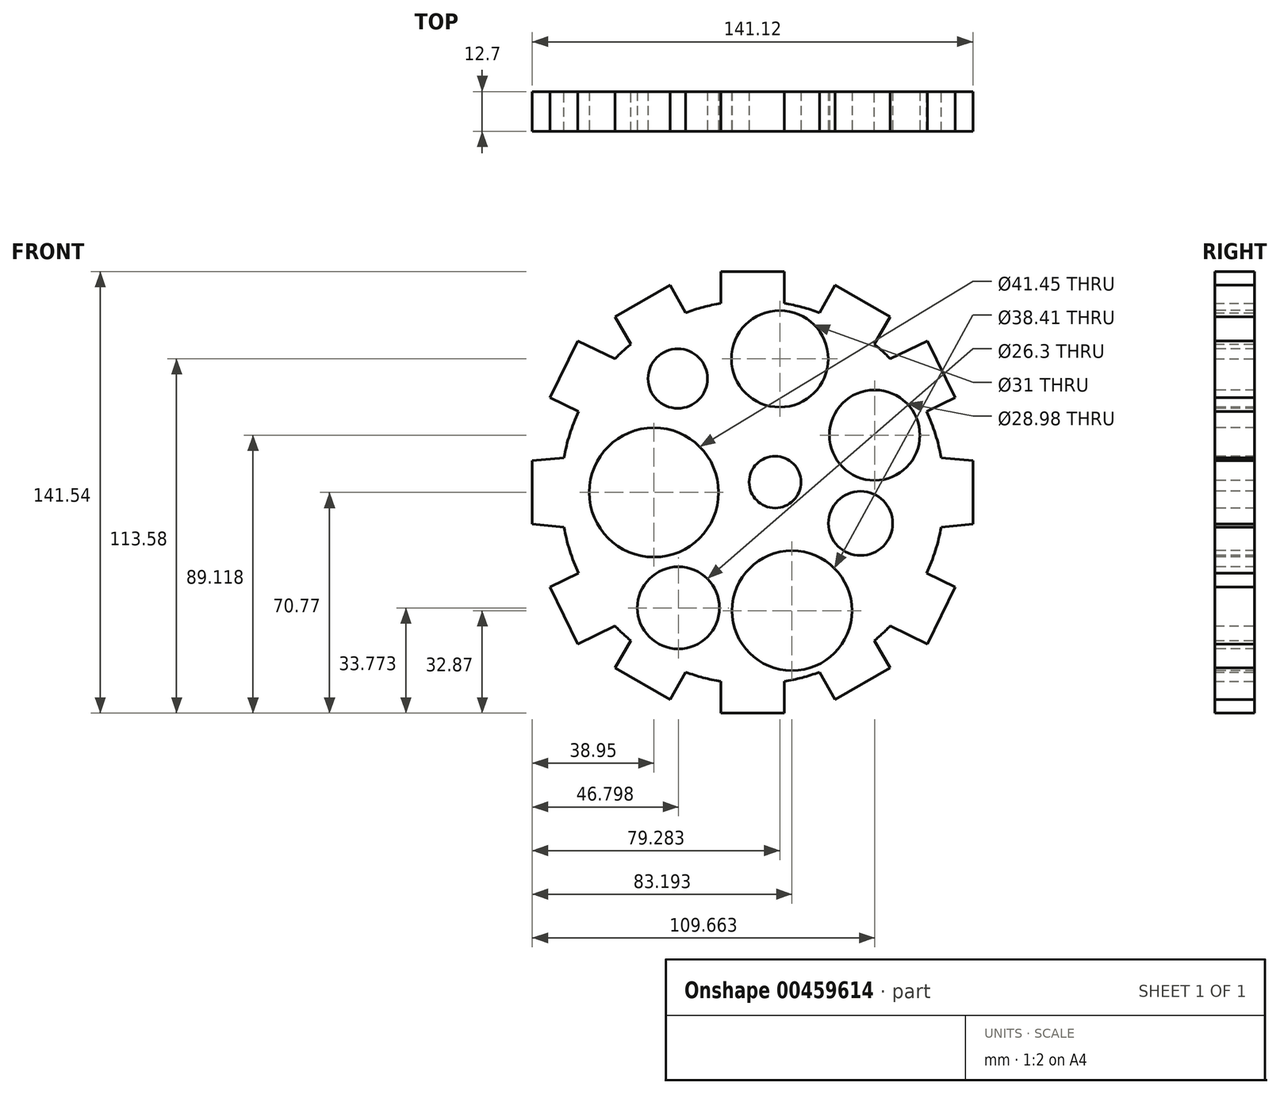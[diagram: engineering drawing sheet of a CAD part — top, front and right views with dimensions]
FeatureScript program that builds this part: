
annotation { "Feature Type Name" : "Feature", "Feature Type Description" : "" }
export const myFeature = defineFeature(function(context is Context, id is Id, definition is map)
    precondition{}
    {
        {
            var Q0;
            Q0=qCreatedBy(makeId("Front.planeOp"),FACE);
            var sketch = newSketch(context, id + "F0", { "sketchPlane" : qUnion([Q0])});
            skArc(sketch, "E0", {"start": v(-55.74, 25.88) * mm, "mid": v(-58.56, 18.64) * mm, "end": v(-60.44, 11.1) * mm});
            skLineSegment(sketch, "E1", {"start": v(-70.56, 0) * mm, "end": v(-70.56, 10.16) * mm});
            skLineSegment(sketch, "E2", {"start": v(-55.74, 25.88) * mm, "end": v(-64.87, 30.33) * mm});
            skLineSegment(sketch, "E3", {"start": v(-64.87, 30.33) * mm, "end": v(-55.97, 48.6) * mm});
            skLineSegment(sketch, "E4", {"start": v(-55.97, 48.6) * mm, "end": v(-44.1, 42.8) * mm});
            skLineSegment(sketch, "E5", {"start": v(-70.56, 10.16) * mm, "end": v(-60.44, 11.1) * mm});
            skLineSegment(sketch, "E6", {"start": v(-39.04, 47.46) * mm, "end": v(-44.1, 56.28) * mm});
            skLineSegment(sketch, "E7", {"start": v(-44.1, 56.28) * mm, "end": v(-26.46, 66.39) * mm});
            skLineSegment(sketch, "E8", {"start": v(-26.46, 66.39) * mm, "end": v(-21.42, 57.6) * mm});
            skArc(sketch, "E9.trimOffspring", {"start": v(-39.04, 47.46) * mm, "mid": v(-41.63, 45.2) * mm, "end": v(-44.1, 42.8) * mm});
            skLineSegment(sketch, "E10", {"start": v(-10.16, 60.6) * mm, "end": v(-10.16, 70.77) * mm});
            skLineSegment(sketch, "E11", {"start": v(-10.16, 70.77) * mm, "end": v(0, 70.77) * mm});
            skLineSegment(sketch, "E12.MirrorCS", {"start": v(10.16, 70.77) * mm, "end": v(0, 70.77) * mm});
            skLineSegment(sketch, "E13.MirrorCS", {"start": v(10.16, 60.6) * mm, "end": v(10.16, 70.77) * mm});
            skLineSegment(sketch, "E14.MirrorCS", {"start": v(44.1, 56.28) * mm, "end": v(26.46, 66.39) * mm});
            skLineSegment(sketch, "E15.MirrorCS", {"start": v(26.46, 66.39) * mm, "end": v(21.42, 57.6) * mm});
            skLineSegment(sketch, "E16.MirrorCS", {"start": v(39.04, 47.46) * mm, "end": v(44.1, 56.28) * mm});
            skLineSegment(sketch, "E17.MirrorCS", {"start": v(55.97, 48.6) * mm, "end": v(44.1, 42.8) * mm});
            skLineSegment(sketch, "E18.MirrorCS", {"start": v(64.87, 30.33) * mm, "end": v(55.97, 48.6) * mm});
            skLineSegment(sketch, "E19.MirrorCS", {"start": v(55.74, 25.88) * mm, "end": v(64.87, 30.33) * mm});
            skArc(sketch, "E20.MirrorCS", {"start": v(55.74, 25.88) * mm, "mid": v(58.56, 18.64) * mm, "end": v(60.44, 11.1) * mm});
            skLineSegment(sketch, "E21.MirrorCS", {"start": v(70.56, 10.16) * mm, "end": v(60.44, 11.1) * mm});
            skLineSegment(sketch, "E22.MirrorCS", {"start": v(70.56, 0) * mm, "end": v(70.56, 10.16) * mm});
            skArc(sketch, "E23.trimOffspring", {"start": v(-44.1, 42.8) * mm, "mid": v(-41.63, 45.2) * mm, "end": v(-39.04, 47.46) * mm});
            skArc(sketch, "E24.trimOffspring", {"start": v(-21.42, 57.6) * mm, "mid": v(-15.86, 59.37) * mm, "end": v(-10.16, 60.6) * mm});
            skArc(sketch, "E25.trimOffspring", {"start": v(-10.16, 60.6) * mm, "mid": v(-15.86, 59.37) * mm, "end": v(-21.42, 57.6) * mm});
            skArc(sketch, "E26.trimOffspring", {"start": v(21.42, 57.6) * mm, "mid": v(15.86, 59.37) * mm, "end": v(10.16, 60.6) * mm});
            skArc(sketch, "E27.trimOffspring", {"start": v(44.1, 42.8) * mm, "mid": v(41.63, 45.2) * mm, "end": v(39.04, 47.46) * mm});
            skLineSegment(sketch, "E28.MirrorCS", {"start": v(-70.56, 0) * mm, "end": v(-70.56, -10.16) * mm});
            skLineSegment(sketch, "E29.MirrorCS", {"start": v(-70.56, -10.16) * mm, "end": v(-60.44, -11.1) * mm});
            skLineSegment(sketch, "E30.MirrorCS", {"start": v(-55.74, -25.88) * mm, "end": v(-64.87, -30.33) * mm});
            skLineSegment(sketch, "E31.MirrorCS", {"start": v(-64.87, -30.33) * mm, "end": v(-55.97, -48.6) * mm});
            skLineSegment(sketch, "E32.MirrorCS", {"start": v(-55.97, -48.6) * mm, "end": v(-44.1, -42.8) * mm});
            skLineSegment(sketch, "E33.MirrorCS", {"start": v(-39.04, -47.46) * mm, "end": v(-44.1, -56.28) * mm});
            skLineSegment(sketch, "E34.MirrorCS", {"start": v(-44.1, -56.28) * mm, "end": v(-26.46, -66.39) * mm});
            skLineSegment(sketch, "E35.MirrorCS", {"start": v(-26.46, -66.39) * mm, "end": v(-21.42, -57.6) * mm});
            skLineSegment(sketch, "E36.MirrorCS", {"start": v(-10.16, -60.6) * mm, "end": v(-10.16, -70.77) * mm});
            skLineSegment(sketch, "E37.MirrorCS", {"start": v(-10.16, -70.77) * mm, "end": v(0, -70.77) * mm});
            skLineSegment(sketch, "E38.MirrorCS", {"start": v(10.16, -70.77) * mm, "end": v(0, -70.77) * mm});
            skLineSegment(sketch, "E39.MirrorCS", {"start": v(10.16, -60.6) * mm, "end": v(10.16, -70.77) * mm});
            skLineSegment(sketch, "E40.MirrorCS", {"start": v(26.46, -66.39) * mm, "end": v(21.42, -57.6) * mm});
            skLineSegment(sketch, "E41.MirrorCS", {"start": v(44.1, -56.28) * mm, "end": v(26.46, -66.39) * mm});
            skLineSegment(sketch, "E42.MirrorCS", {"start": v(39.04, -47.46) * mm, "end": v(44.1, -56.28) * mm});
            skLineSegment(sketch, "E43.MirrorCS", {"start": v(55.97, -48.6) * mm, "end": v(44.1, -42.8) * mm});
            skLineSegment(sketch, "E44.MirrorCS", {"start": v(64.87, -30.33) * mm, "end": v(55.97, -48.6) * mm});
            skLineSegment(sketch, "E45.MirrorCS", {"start": v(55.74, -25.88) * mm, "end": v(64.87, -30.33) * mm});
            skLineSegment(sketch, "E46.MirrorCS", {"start": v(70.56, -10.16) * mm, "end": v(60.44, -11.1) * mm});
            skLineSegment(sketch, "E47.MirrorCS", {"start": v(70.56, 0) * mm, "end": v(70.56, -10.16) * mm});
            skArc(sketch, "E48.trimOffspring", {"start": v(-60.44, 11.1) * mm, "mid": v(-58.56, 18.64) * mm, "end": v(-55.74, 25.88) * mm});
            skArc(sketch, "E49.trimOffspring", {"start": v(-60.44, -11.1) * mm, "mid": v(-58.56, -18.64) * mm, "end": v(-55.74, -25.88) * mm});
            skArc(sketch, "E50.trimOffspring", {"start": v(-55.74, -25.88) * mm, "mid": v(-58.56, -18.64) * mm, "end": v(-60.44, -11.1) * mm});
            skArc(sketch, "E51.trimOffspring", {"start": v(-44.1, -42.8) * mm, "mid": v(-41.63, -45.2) * mm, "end": v(-39.04, -47.46) * mm});
            skArc(sketch, "E52.trimOffspring", {"start": v(-21.42, -57.6) * mm, "mid": v(-15.86, -59.37) * mm, "end": v(-10.16, -60.6) * mm});
            skArc(sketch, "E53.trimOffspring", {"start": v(10.16, -60.6) * mm, "mid": v(15.86, -59.37) * mm, "end": v(21.42, -57.6) * mm});
            skArc(sketch, "E54.trimOffspring", {"start": v(-10.16, -60.6) * mm, "mid": v(-15.86, -59.37) * mm, "end": v(-21.42, -57.6) * mm});
            skArc(sketch, "E55.trimOffspring", {"start": v(21.42, -57.6) * mm, "mid": v(15.86, -59.37) * mm, "end": v(10.16, -60.6) * mm});
            skArc(sketch, "E56.trimOffspring", {"start": v(44.1, -42.8) * mm, "mid": v(41.63, -45.2) * mm, "end": v(39.04, -47.46) * mm});
            skArc(sketch, "E57.trimOffspring", {"start": v(39.04, -47.46) * mm, "mid": v(41.63, -45.2) * mm, "end": v(44.1, -42.8) * mm});
            skArc(sketch, "E58.trimOffspring", {"start": v(55.74, -25.88) * mm, "mid": v(58.56, -18.64) * mm, "end": v(60.44, -11.1) * mm});
            skArc(sketch, "E59.trimOffspring", {"start": v(60.44, -11.1) * mm, "mid": v(58.56, -18.64) * mm, "end": v(55.74, -25.88) * mm});
            skArc(sketch, "E60.trimOffspring", {"start": v(60.44, 11.1) * mm, "mid": v(58.56, 18.64) * mm, "end": v(55.74, 25.88) * mm});
            skArc(sketch, "E61.trimOffspring", {"start": v(10.16, 60.6) * mm, "mid": v(15.86, 59.37) * mm, "end": v(21.42, 57.6) * mm});
            skLineSegment(sketch, "E62.trimOffspring", {"start": v(0, -70.77) * mm, "end": v(0, -71.89) * mm, "construction": true});
            skPoint(sketch, "E63.start.orphan", {"position": v(0, 76.4) * mm});
            skPoint(sketch, "E64.start.orphan", {"position": v(-89.94, 0) * mm});
            skSolve(sketch);
        }
        {
            var Q0;
            Q0 = qSketchRegion(id + "F0", true);
            extrude(context, id + "F1", {"entities" : qUnion([Q0]), "depth" : 12.7 * mm});
        }
        {
            var Q0;
            Q0=makeQuery(id+"F1.opExtrude","CAP_FACE",FACE,{"disambiguationData":[OSD([sQuery(id+"F0.wireOp",EDGE,"E1"),sQuery(id+"F0.wireOp",EDGE,"E2"),sQuery(id+"F0.wireOp",EDGE,"E3"),sQuery(id+"F0.wireOp",EDGE,"E4"),sQuery(id+"F0.wireOp",EDGE,"E5"),sQuery(id+"F0.wireOp",EDGE,"E6"),sQuery(id+"F0.wireOp",EDGE,"E7"),sQuery(id+"F0.wireOp",EDGE,"E8"),sQuery(id+"F0.wireOp",EDGE,"E10"),sQuery(id+"F0.wireOp",EDGE,"E11"),sQuery(id+"F0.wireOp",EDGE,"E12.MirrorCS"),sQuery(id+"F0.wireOp",EDGE,"E13.MirrorCS"),sQuery(id+"F0.wireOp",EDGE,"E14.MirrorCS"),sQuery(id+"F0.wireOp",EDGE,"E15.MirrorCS"),sQuery(id+"F0.wireOp",EDGE,"E16.MirrorCS"),sQuery(id+"F0.wireOp",EDGE,"E17.MirrorCS"),sQuery(id+"F0.wireOp",EDGE,"E18.MirrorCS"),sQuery(id+"F0.wireOp",EDGE,"E19.MirrorCS"),sQuery(id+"F0.wireOp",EDGE,"E21.MirrorCS"),sQuery(id+"F0.wireOp",EDGE,"E22.MirrorCS"),sQuery(id+"F0.wireOp",EDGE,"E23.trimOffspring"),sQuery(id+"F0.wireOp",EDGE,"E25.trimOffspring"),sQuery(id+"F0.wireOp",EDGE,"E27.trimOffspring"),sQuery(id+"F0.wireOp",EDGE,"E28.MirrorCS"),sQuery(id+"F0.wireOp",EDGE,"E29.MirrorCS"),sQuery(id+"F0.wireOp",EDGE,"E30.MirrorCS"),sQuery(id+"F0.wireOp",EDGE,"E31.MirrorCS"),sQuery(id+"F0.wireOp",EDGE,"E32.MirrorCS"),sQuery(id+"F0.wireOp",EDGE,"E33.MirrorCS"),sQuery(id+"F0.wireOp",EDGE,"E34.MirrorCS"),sQuery(id+"F0.wireOp",EDGE,"E35.MirrorCS"),sQuery(id+"F0.wireOp",EDGE,"E36.MirrorCS"),sQuery(id+"F0.wireOp",EDGE,"E37.MirrorCS"),sQuery(id+"F0.wireOp",EDGE,"E38.MirrorCS"),sQuery(id+"F0.wireOp",EDGE,"E39.MirrorCS"),sQuery(id+"F0.wireOp",EDGE,"E40.MirrorCS"),sQuery(id+"F0.wireOp",EDGE,"E41.MirrorCS"),sQuery(id+"F0.wireOp",EDGE,"E42.MirrorCS"),sQuery(id+"F0.wireOp",EDGE,"E43.MirrorCS"),sQuery(id+"F0.wireOp",EDGE,"E44.MirrorCS"),sQuery(id+"F0.wireOp",EDGE,"E45.MirrorCS"),sQuery(id+"F0.wireOp",EDGE,"E46.MirrorCS"),sQuery(id+"F0.wireOp",EDGE,"E47.MirrorCS"),sQuery(id+"F0.wireOp",EDGE,"E48.trimOffspring"),sQuery(id+"F0.wireOp",EDGE,"E50.trimOffspring"),sQuery(id+"F0.wireOp",EDGE,"E51.trimOffspring"),sQuery(id+"F0.wireOp",EDGE,"E54.trimOffspring"),sQuery(id+"F0.wireOp",EDGE,"E55.trimOffspring"),sQuery(id+"F0.wireOp",EDGE,"E57.trimOffspring"),sQuery(id+"F0.wireOp",EDGE,"E59.trimOffspring"),sQuery(id+"F0.wireOp",EDGE,"E60.trimOffspring"),sQuery(id+"F0.wireOp",EDGE,"E61.trimOffspring")])],"isStart":false});
            var sketch = newSketch(context, id + "F2", { "sketchPlane" : qUnion([Q0])});
            skLineSegment(sketch, "E65", {"start": v(0, 91.04) * mm, "end": v(0, -92.83) * mm, "construction": true});
            skLineSegment(sketch, "E66", {"start": v(-95.47, 0) * mm, "end": v(102.1, 0) * mm, "construction": true});
            skArc(sketch, "E67", {"start": v(-10.88, 0) * mm, "mid": v(-31.61, 20.73) * mm, "end": v(-52.34, 0) * mm});
            skArc(sketch, "E68.MirrorCS", {"start": v(-10.88, 0) * mm, "mid": v(-31.61, -20.73) * mm, "end": v(-52.34, 0) * mm});
            skSolve(sketch);
        }
        {
            var Q0;
            Q0=makeQuery(id+"F2.imprint","IMPRINT",FACE,{"disambiguationData":[TD([[makeQuery(id+"F2.imprint","IMPRINT",EDGE,{"derivedFrom":sQuery(id+"F2.wireOp",EDGE,"E67")}),1.0]])]});
            extrude(context, id + "F3", {"entities" : qUnion([Q0]), "operationType" : NewBodyOperationType.REMOVE, "oppositeDirection" : true, "depth" : 25.4 * mm});
        }
        {
            var Q0;
            Q0 = qSketchRegion(id + "F2", true);
            extrude(context, id + "F4", {"entities" : qUnion([Q0]), "operationType" : NewBodyOperationType.REMOVE, "oppositeDirection" : true, "depth" : 25.4 * mm});
        }
        {
            var Q0;
            Q0=makeQuery(id+"F1.opExtrude","CAP_FACE",FACE,{"disambiguationData":[OSD([sQuery(id+"F0.wireOp",EDGE,"E1"),sQuery(id+"F0.wireOp",EDGE,"E2"),sQuery(id+"F0.wireOp",EDGE,"E3"),sQuery(id+"F0.wireOp",EDGE,"E4"),sQuery(id+"F0.wireOp",EDGE,"E5"),sQuery(id+"F0.wireOp",EDGE,"E6"),sQuery(id+"F0.wireOp",EDGE,"E7"),sQuery(id+"F0.wireOp",EDGE,"E8"),sQuery(id+"F0.wireOp",EDGE,"E10"),sQuery(id+"F0.wireOp",EDGE,"E11"),sQuery(id+"F0.wireOp",EDGE,"E12.MirrorCS"),sQuery(id+"F0.wireOp",EDGE,"E13.MirrorCS"),sQuery(id+"F0.wireOp",EDGE,"E14.MirrorCS"),sQuery(id+"F0.wireOp",EDGE,"E15.MirrorCS"),sQuery(id+"F0.wireOp",EDGE,"E16.MirrorCS"),sQuery(id+"F0.wireOp",EDGE,"E17.MirrorCS"),sQuery(id+"F0.wireOp",EDGE,"E18.MirrorCS"),sQuery(id+"F0.wireOp",EDGE,"E19.MirrorCS"),sQuery(id+"F0.wireOp",EDGE,"E21.MirrorCS"),sQuery(id+"F0.wireOp",EDGE,"E22.MirrorCS"),sQuery(id+"F0.wireOp",EDGE,"E23.trimOffspring"),sQuery(id+"F0.wireOp",EDGE,"E25.trimOffspring"),sQuery(id+"F0.wireOp",EDGE,"E27.trimOffspring"),sQuery(id+"F0.wireOp",EDGE,"E28.MirrorCS"),sQuery(id+"F0.wireOp",EDGE,"E29.MirrorCS"),sQuery(id+"F0.wireOp",EDGE,"E30.MirrorCS"),sQuery(id+"F0.wireOp",EDGE,"E31.MirrorCS"),sQuery(id+"F0.wireOp",EDGE,"E32.MirrorCS"),sQuery(id+"F0.wireOp",EDGE,"E33.MirrorCS"),sQuery(id+"F0.wireOp",EDGE,"E34.MirrorCS"),sQuery(id+"F0.wireOp",EDGE,"E35.MirrorCS"),sQuery(id+"F0.wireOp",EDGE,"E36.MirrorCS"),sQuery(id+"F0.wireOp",EDGE,"E37.MirrorCS"),sQuery(id+"F0.wireOp",EDGE,"E38.MirrorCS"),sQuery(id+"F0.wireOp",EDGE,"E39.MirrorCS"),sQuery(id+"F0.wireOp",EDGE,"E40.MirrorCS"),sQuery(id+"F0.wireOp",EDGE,"E41.MirrorCS"),sQuery(id+"F0.wireOp",EDGE,"E42.MirrorCS"),sQuery(id+"F0.wireOp",EDGE,"E43.MirrorCS"),sQuery(id+"F0.wireOp",EDGE,"E44.MirrorCS"),sQuery(id+"F0.wireOp",EDGE,"E45.MirrorCS"),sQuery(id+"F0.wireOp",EDGE,"E46.MirrorCS"),sQuery(id+"F0.wireOp",EDGE,"E47.MirrorCS"),sQuery(id+"F0.wireOp",EDGE,"E48.trimOffspring"),sQuery(id+"F0.wireOp",EDGE,"E50.trimOffspring"),sQuery(id+"F0.wireOp",EDGE,"E51.trimOffspring"),sQuery(id+"F0.wireOp",EDGE,"E54.trimOffspring"),sQuery(id+"F0.wireOp",EDGE,"E55.trimOffspring"),sQuery(id+"F0.wireOp",EDGE,"E57.trimOffspring"),sQuery(id+"F0.wireOp",EDGE,"E59.trimOffspring"),sQuery(id+"F0.wireOp",EDGE,"E60.trimOffspring"),sQuery(id+"F0.wireOp",EDGE,"E61.trimOffspring")])],"isStart":false});
            var sketch = newSketch(context, id + "F5", { "sketchPlane" : qUnion([Q0])});
            skCircle(sketch, "E69", {"center": v(-23.95, 36.49) * mm, "radius": 9.53 * mm});
            skCircle(sketch, "E70", {"center": v(8.72, 42.8) * mm, "radius": 15.5 * mm});
            skCircle(sketch, "E71", {"center": v(-23.76, -37) * mm, "radius": 13.15 * mm});
            skCircle(sketch, "E72", {"center": v(12.63, -37.9) * mm, "radius": 19.2 * mm});
            skCircle(sketch, "E73", {"center": v(7.22, 3.3) * mm, "radius": 8.32 * mm});
            skSolve(sketch);
        }
        {
            var Q0;
            Q0 = qSketchRegion(id + "F5", true);
            extrude(context, id + "F6", {"entities" : qUnion([Q0]), "operationType" : NewBodyOperationType.REMOVE, "oppositeDirection" : true, "depth" : 25.4 * mm});
        }
        {
            var Q0;
            Q0=makeQuery(id+"F1.opExtrude","CAP_FACE",FACE,{"disambiguationData":[OSD([sQuery(id+"F0.wireOp",EDGE,"E1"),sQuery(id+"F0.wireOp",EDGE,"E2"),sQuery(id+"F0.wireOp",EDGE,"E3"),sQuery(id+"F0.wireOp",EDGE,"E4"),sQuery(id+"F0.wireOp",EDGE,"E5"),sQuery(id+"F0.wireOp",EDGE,"E6"),sQuery(id+"F0.wireOp",EDGE,"E7"),sQuery(id+"F0.wireOp",EDGE,"E8"),sQuery(id+"F0.wireOp",EDGE,"E10"),sQuery(id+"F0.wireOp",EDGE,"E11"),sQuery(id+"F0.wireOp",EDGE,"E12.MirrorCS"),sQuery(id+"F0.wireOp",EDGE,"E13.MirrorCS"),sQuery(id+"F0.wireOp",EDGE,"E14.MirrorCS"),sQuery(id+"F0.wireOp",EDGE,"E15.MirrorCS"),sQuery(id+"F0.wireOp",EDGE,"E16.MirrorCS"),sQuery(id+"F0.wireOp",EDGE,"E17.MirrorCS"),sQuery(id+"F0.wireOp",EDGE,"E18.MirrorCS"),sQuery(id+"F0.wireOp",EDGE,"E19.MirrorCS"),sQuery(id+"F0.wireOp",EDGE,"E21.MirrorCS"),sQuery(id+"F0.wireOp",EDGE,"E22.MirrorCS"),sQuery(id+"F0.wireOp",EDGE,"E23.trimOffspring"),sQuery(id+"F0.wireOp",EDGE,"E25.trimOffspring"),sQuery(id+"F0.wireOp",EDGE,"E27.trimOffspring"),sQuery(id+"F0.wireOp",EDGE,"E28.MirrorCS"),sQuery(id+"F0.wireOp",EDGE,"E29.MirrorCS"),sQuery(id+"F0.wireOp",EDGE,"E30.MirrorCS"),sQuery(id+"F0.wireOp",EDGE,"E31.MirrorCS"),sQuery(id+"F0.wireOp",EDGE,"E32.MirrorCS"),sQuery(id+"F0.wireOp",EDGE,"E33.MirrorCS"),sQuery(id+"F0.wireOp",EDGE,"E34.MirrorCS"),sQuery(id+"F0.wireOp",EDGE,"E35.MirrorCS"),sQuery(id+"F0.wireOp",EDGE,"E36.MirrorCS"),sQuery(id+"F0.wireOp",EDGE,"E37.MirrorCS"),sQuery(id+"F0.wireOp",EDGE,"E38.MirrorCS"),sQuery(id+"F0.wireOp",EDGE,"E39.MirrorCS"),sQuery(id+"F0.wireOp",EDGE,"E40.MirrorCS"),sQuery(id+"F0.wireOp",EDGE,"E41.MirrorCS"),sQuery(id+"F0.wireOp",EDGE,"E42.MirrorCS"),sQuery(id+"F0.wireOp",EDGE,"E43.MirrorCS"),sQuery(id+"F0.wireOp",EDGE,"E44.MirrorCS"),sQuery(id+"F0.wireOp",EDGE,"E45.MirrorCS"),sQuery(id+"F0.wireOp",EDGE,"E46.MirrorCS"),sQuery(id+"F0.wireOp",EDGE,"E47.MirrorCS"),sQuery(id+"F0.wireOp",EDGE,"E48.trimOffspring"),sQuery(id+"F0.wireOp",EDGE,"E50.trimOffspring"),sQuery(id+"F0.wireOp",EDGE,"E51.trimOffspring"),sQuery(id+"F0.wireOp",EDGE,"E54.trimOffspring"),sQuery(id+"F0.wireOp",EDGE,"E55.trimOffspring"),sQuery(id+"F0.wireOp",EDGE,"E57.trimOffspring"),sQuery(id+"F0.wireOp",EDGE,"E59.trimOffspring"),sQuery(id+"F0.wireOp",EDGE,"E60.trimOffspring"),sQuery(id+"F0.wireOp",EDGE,"E61.trimOffspring")])],"isStart":false});
            var sketch = newSketch(context, id + "F7", { "sketchPlane" : qUnion([Q0])});
            skCircle(sketch, "E74", {"center": v(39.1, 18.35) * mm, "radius": 14.5 * mm});
            skCircle(sketch, "E75", {"center": v(34.6, -9.93) * mm, "radius": 10.28 * mm});
            skSolve(sketch);
        }
        {
            var Q0;
            Q0 = qSketchRegion(id + "F7", true);
            extrude(context, id + "F8", {"entities" : qUnion([Q0]), "operationType" : NewBodyOperationType.REMOVE, "oppositeDirection" : true, "depth" : 25.4 * mm});
        }
    });
